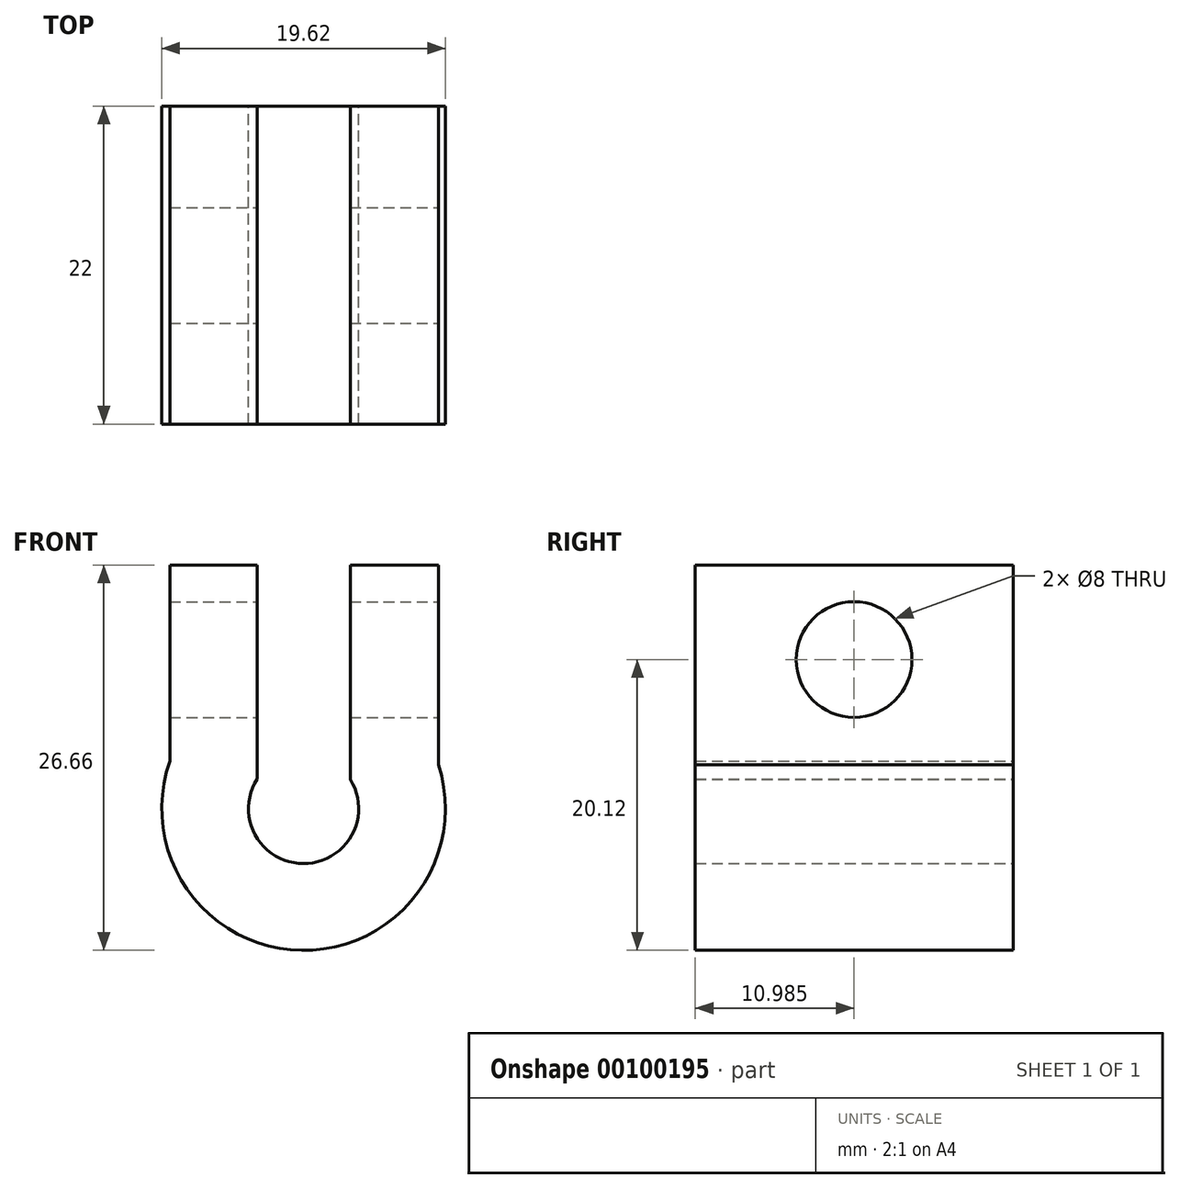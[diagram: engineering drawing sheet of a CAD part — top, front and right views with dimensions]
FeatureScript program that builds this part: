
annotation { "Feature Type Name" : "Feature", "Feature Type Description" : "" }
export const myFeature = defineFeature(function(context is Context, id is Id, definition is map)
    precondition{}
    {
        {
            var Q0;
            Q0=qCreatedBy(makeId("Front.planeOp"),FACE);
            var sketch = newSketch(context, id + "F0", { "sketchPlane" : qUnion([Q0])});
            skArc(sketch, "E0", {"start": v(-3.22, 2.04) * mm, "mid": v(-0.02, -3.8) * mm, "end": v(3.23, 2.02) * mm});
            skArc(sketch, "E1.0", {"start": v(-9.25, 3.27) * mm, "mid": v(-0.13, -9.8) * mm, "end": v(9.33, 3.03) * mm});
            skLineSegment(sketch, "E2.0", {"start": v(3.23, 2.02) * mm, "end": v(3.23, 16.85) * mm});
            skLineSegment(sketch, "E3.0", {"start": v(-3.22, 2.04) * mm, "end": v(-3.22, 16.85) * mm});
            skPoint(sketch, "E4.start.orphan", {"position": v(0, 3.81) * mm});
            skLineSegment(sketch, "E5", {"start": v(9.33, 3.03) * mm, "end": v(9.33, 16.85) * mm});
            skLineSegment(sketch, "E6", {"start": v(9.33, 16.85) * mm, "end": v(3.23, 16.85) * mm});
            skLineSegment(sketch, "E7", {"start": v(-9.25, 3.27) * mm, "end": v(-9.25, 16.85) * mm});
            skLineSegment(sketch, "E8", {"start": v(-9.25, 16.85) * mm, "end": v(-3.22, 16.85) * mm});
            skPoint(sketch, "E9.orphan", {"position": v(-1.42, 16.85) * mm});
            skSolve(sketch);
        }
        {
            var Q0;
            Q0 = qSketchRegion(id + "F0", true);
            extrude(context, id + "F1", {"entities" : qUnion([Q0]), "depth" : 22 * mm});
        }
        {
            var Q0;
            Q0=makeQuery(id+"F1.opExtrude","SWEPT_FACE",FACE,{"disambiguationData":[OSD([sQuery(id+"F0.wireOp",EDGE,"E5")])]});
            var sketch = newSketch(context, id + "F2", { "sketchPlane" : qUnion([Q0])});
            skCircle(sketch, "E10", {"center": v(-11.01, 10.3) * mm, "radius": 4 * mm});
            skSolve(sketch);
        }
        {
            var Q0;
            Q0 = qSketchRegion(id + "F2", true);
            var Q1;
            Q1=makeQuery(id+"F1.opExtrude","SWEPT_FACE",FACE,{"disambiguationData":[OSD([sQuery(id+"F0.wireOp",EDGE,"E7")])]});
            extrude(context, id + "F3", {"entities" : qUnion([Q0]), "operationType" : NewBodyOperationType.REMOVE, "endBound" : BoundingType.UP_TO_SURFACE, "oppositeDirection" : true, "endBoundEntityFace" : qUnion([Q1]), "depth" : 25.4 * mm});
        }
    });
